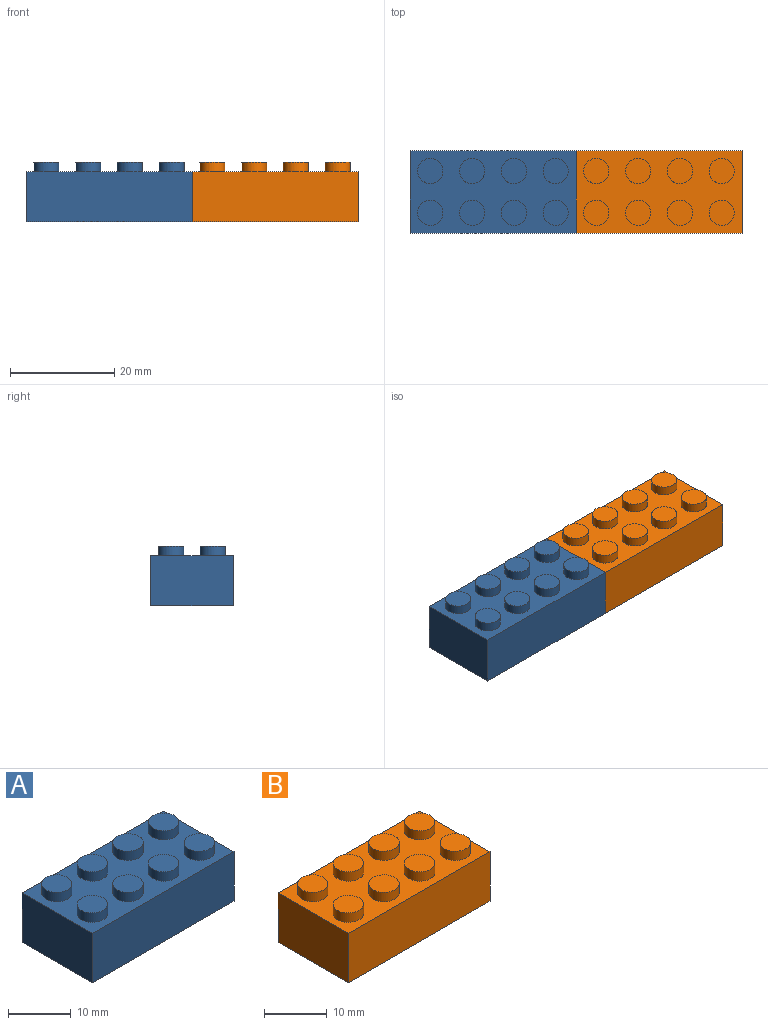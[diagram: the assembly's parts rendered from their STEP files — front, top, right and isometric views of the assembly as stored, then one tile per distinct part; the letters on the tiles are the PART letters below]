
ASSEMBLY  parts=2 mates=1
PART A: 27 faces, bbox 31.8x15.8x11.4 mm
  f0: plane 31.8x9.6mm, normal (0,1,0), area 305.3mm2, adj f1,f3,f4,f5
  f1: plane 15.8x9.6mm, normal (-1,0,0), area 151.7mm2, adj f0,f2,f4,f5
  f2: plane 31.8x9.6mm, normal (0,-1,0), area 305.3mm2, adj f1,f3,f4,f5
  f3: plane 15.8x9.6mm, normal (1,0,0), area 151.7mm2, adj f0,f2,f4,f5
  f4: plane 31.8x15.8mm, normal (0,0,1), area 355.3mm2, adj f0,f1,f2,f3,f6,f8,f10,f12
  f5: plane 31.8x15.8mm, normal (0,0,-1), area 129.6mm2, adj f0,f1,f2,f3,f22,f23,f24,f25
  f6: cylinder r=2.42mm len=4.84mm, axis (0,0,-1), area 27.4mm2, adj f4,f7
  f7: plane 4.84x4.84mm, normal (0,0,1), area 18.4mm2, adj f6
  f8: cylinder r=2.42mm len=4.84mm, axis (0,0,-1), area 27.4mm2, adj f4,f9
  f9: plane 4.84x4.84mm, normal (0,0,1), area 18.4mm2, adj f8
  f10: cylinder r=2.42mm len=4.84mm, axis (0,0,-1), area 27.4mm2, adj f4,f11
  f11: plane 4.84x4.84mm, normal (0,0,1), area 18.4mm2, adj f10
  f12: cylinder r=2.42mm len=4.84mm, axis (0,0,-1), area 27.4mm2, adj f4,f13
  f13: plane 4.84x4.84mm, normal (0,0,1), area 18.4mm2, adj f12
  f14: cylinder r=2.42mm len=4.84mm, axis (0,0,-1), area 27.4mm2, adj f4,f15
  f15: plane 4.84x4.84mm, normal (0,0,1), area 18.4mm2, adj f14
  f16: cylinder r=2.42mm len=4.84mm, axis (0,0,-1), area 27.4mm2, adj f4,f17
  f17: plane 4.84x4.84mm, normal (0,0,1), area 18.4mm2, adj f16
  f18: cylinder r=2.42mm len=4.84mm, axis (0,0,-1), area 27.4mm2, adj f4,f19
  f19: plane 4.84x4.84mm, normal (0,0,1), area 18.4mm2, adj f18
  f20: cylinder r=2.42mm len=4.84mm, axis (0,0,-1), area 27.4mm2, adj f4,f21
  f21: plane 4.84x4.84mm, normal (0,0,1), area 18.4mm2, adj f20
  f22: plane 12.9x8.6mm, normal (1,0,0), area 110.9mm2, adj f5,f23,f25,f26
  f23: plane 28.9x8.6mm, normal (0,1,0), area 248.5mm2, adj f5,f22,f24,f26
  f24: plane 12.9x8.6mm, normal (-1,0,0), area 110.9mm2, adj f5,f23,f25,f26
  f25: plane 28.9x8.6mm, normal (0,-1,0), area 248.5mm2, adj f5,f22,f24,f26
  f26: plane 28.9x12.9mm, normal (0,0,-1), area 372.8mm2, adj f22,f23,f24,f25
PART B: 27 faces, bbox 31.8x15.8x11.4 mm
  f0: plane 31.8x9.6mm, normal (0,1,0), area 305.3mm2, adj f1,f3,f4,f5
  f1: plane 15.8x9.6mm, normal (-1,0,0), area 151.7mm2, adj f0,f2,f4,f5
  f2: plane 31.8x9.6mm, normal (0,-1,0), area 305.3mm2, adj f1,f3,f4,f5
  f3: plane 15.8x9.6mm, normal (1,0,0), area 151.7mm2, adj f0,f2,f4,f5
  f4: plane 31.8x15.8mm, normal (0,0,1), area 355.3mm2, adj f0,f1,f2,f3,f6,f8,f10,f12
  f5: plane 31.8x15.8mm, normal (0,0,-1), area 129.6mm2, adj f0,f1,f2,f3,f22,f23,f24,f25
  f6: cylinder r=2.42mm len=4.84mm, axis (0,0,-1), area 27.4mm2, adj f4,f7
  f7: plane 4.84x4.84mm, normal (0,0,1), area 18.4mm2, adj f6
  f8: cylinder r=2.42mm len=4.84mm, axis (0,0,-1), area 27.4mm2, adj f4,f9
  f9: plane 4.84x4.84mm, normal (0,0,1), area 18.4mm2, adj f8
  f10: cylinder r=2.42mm len=4.84mm, axis (0,0,-1), area 27.4mm2, adj f4,f11
  f11: plane 4.84x4.84mm, normal (0,0,1), area 18.4mm2, adj f10
  f12: cylinder r=2.42mm len=4.84mm, axis (0,0,-1), area 27.4mm2, adj f4,f13
  f13: plane 4.84x4.84mm, normal (0,0,1), area 18.4mm2, adj f12
  f14: cylinder r=2.42mm len=4.84mm, axis (0,0,-1), area 27.4mm2, adj f4,f15
  f15: plane 4.84x4.84mm, normal (0,0,1), area 18.4mm2, adj f14
  f16: cylinder r=2.42mm len=4.84mm, axis (0,0,-1), area 27.4mm2, adj f4,f17
  f17: plane 4.84x4.84mm, normal (0,0,1), area 18.4mm2, adj f16
  f18: cylinder r=2.42mm len=4.84mm, axis (0,0,-1), area 27.4mm2, adj f4,f19
  f19: plane 4.84x4.84mm, normal (0,0,1), area 18.4mm2, adj f18
  f20: cylinder r=2.42mm len=4.84mm, axis (0,0,-1), area 27.4mm2, adj f4,f21
  f21: plane 4.84x4.84mm, normal (0,0,1), area 18.4mm2, adj f20
  f22: plane 12.9x8.6mm, normal (1,0,0), area 110.9mm2, adj f5,f23,f25,f26
  f23: plane 28.9x8.6mm, normal (0,1,0), area 248.5mm2, adj f5,f22,f24,f26
  f24: plane 12.9x8.6mm, normal (-1,0,0), area 110.9mm2, adj f5,f23,f25,f26
  f25: plane 28.9x8.6mm, normal (0,-1,0), area 248.5mm2, adj f5,f22,f24,f26
  f26: plane 28.9x12.9mm, normal (0,0,-1), area 372.8mm2, adj f22,f23,f24,f25
PLACE A t=(-12.29,22.19,-5.1)mm
PLACE B t=(19.51,47.19,-5.1)mm
MATE fastened A.f3 <-> B.f1  axis (1,0,0) through (28.36,13.88,-0.3)mm
